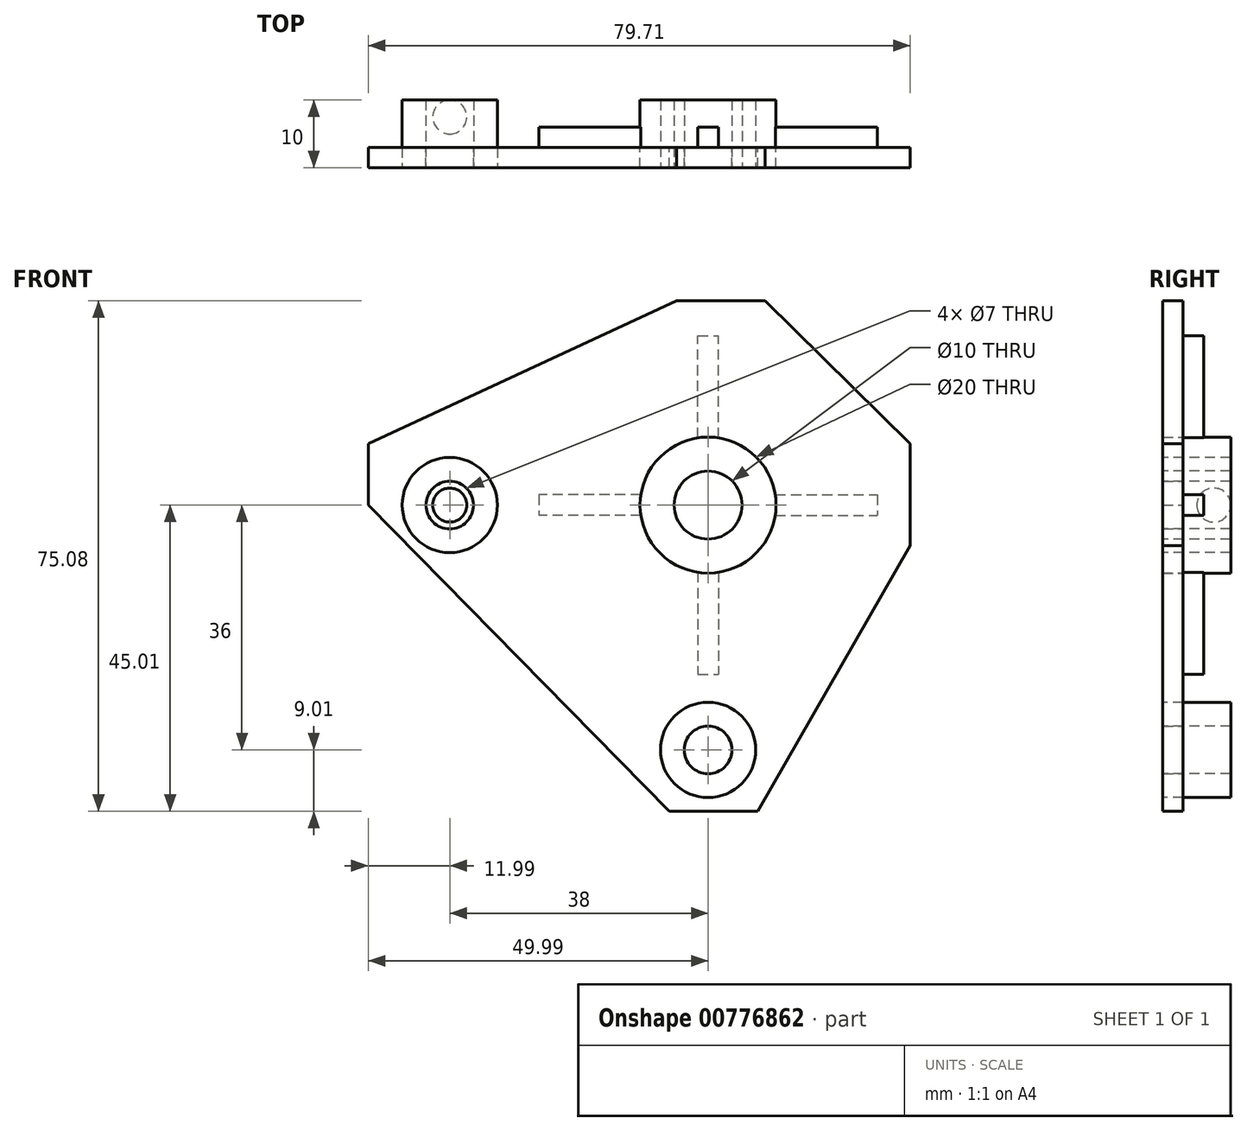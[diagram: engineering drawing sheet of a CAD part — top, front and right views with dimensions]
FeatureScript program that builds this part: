
annotation { "Feature Type Name" : "Feature", "Feature Type Description" : "" }
export const myFeature = defineFeature(function(context is Context, id is Id, definition is map)
    precondition{}
    {
        {
            var Q0;
            Q0=qCreatedBy(makeId("Front.planeOp"),FACE);
            var sketch = newSketch(context, id + "F0", { "sketchPlane" : qUnion([Q0])});
            skCircle(sketch, "E0", {"center": v(0, 0) * mm, "radius": 10 * mm});
            skLineSegment(sketch, "E1", {"start": v(0, 30.64) * mm, "end": v(0, -43.55) * mm, "construction": true});
            skLineSegment(sketch, "E2", {"start": v(-1.5, 9.89) * mm, "end": v(-1.5, 24.89) * mm});
            skLineSegment(sketch, "E3.MirrorCS", {"start": v(1.5, 9.89) * mm, "end": v(1.5, 24.89) * mm});
            skLineSegment(sketch, "E4", {"start": v(-1.5, 24.89) * mm, "end": v(1.5, 24.89) * mm});
            skLineSegment(sketch, "E5", {"start": v(-38, 0) * mm, "end": v(36.67, 0) * mm, "construction": true});
            skLineSegment(sketch, "E6.MirrorCS", {"start": v(1.5, -9.89) * mm, "end": v(1.5, -24.89) * mm});
            skLineSegment(sketch, "E7.MirrorCS", {"start": v(-1.5, -9.89) * mm, "end": v(-1.5, -24.89) * mm});
            skLineSegment(sketch, "E8.MirrorCS", {"start": v(-1.5, -24.89) * mm, "end": v(1.5, -24.89) * mm});
            skLineSegment(sketch, "E9", {"start": v(9.89, 1.5) * mm, "end": v(24.89, 1.5) * mm});
            skLineSegment(sketch, "E10.MirrorCS", {"start": v(9.89, -1.5) * mm, "end": v(24.89, -1.5) * mm});
            skLineSegment(sketch, "E11", {"start": v(24.89, 1.5) * mm, "end": v(24.89, -1.5) * mm});
            skLineSegment(sketch, "E12.MirrorCS", {"start": v(-9.89, 1.5) * mm, "end": v(-24.89, 1.5) * mm});
            skLineSegment(sketch, "E13.MirrorCS", {"start": v(-9.89, -1.5) * mm, "end": v(-24.89, -1.5) * mm});
            skLineSegment(sketch, "E14.MirrorCS", {"start": v(-24.89, 1.5) * mm, "end": v(-24.89, -1.5) * mm});
            skCircle(sketch, "E15", {"center": v(-38, 0) * mm, "radius": 3.5 * mm});
            skCircle(sketch, "E16", {"center": v(0, -36) * mm, "radius": 3.5 * mm});
            skLineSegment(sketch, "E17", {"start": v(-49.99, 0) * mm, "end": v(-5.7, -45.01) * mm});
            skLineSegment(sketch, "E18", {"start": v(-5.7, -45.01) * mm, "end": v(7.3, -45.01) * mm});
            skLineSegment(sketch, "E19", {"start": v(7.3, -45.01) * mm, "end": v(29.72, -6) * mm});
            skLineSegment(sketch, "E20", {"start": v(29.72, 2.8) * mm, "end": v(29.72, 9) * mm});
            skLineSegment(sketch, "E21", {"start": v(29.72, 9) * mm, "end": v(8.36, 30.07) * mm});
            skLineSegment(sketch, "E22", {"start": v(8.36, 30.07) * mm, "end": v(-4.64, 30.07) * mm});
            skLineSegment(sketch, "E23", {"start": v(-4.64, 30.07) * mm, "end": v(-49.99, 9) * mm});
            skLineSegment(sketch, "E24", {"start": v(-49.99, 9) * mm, "end": v(-49.99, 0) * mm});
            skLineSegment(sketch, "E25", {"start": v(29.72, 2.8) * mm, "end": v(29.72, -6) * mm});
            skSolve(sketch);
        }
        {
            var Q0;
            {var subQ0=sQuery(id+"F0.wireOp",EDGE,"E12.MirrorCS");Q0=makeQuery(id+"F0.imprint","IMPRINT",FACE,{"disambiguationData":[TD([[makeQuery(id+"F0.imprint","IMPRINT",EDGE,{"derivedFrom":subQ0}),1.0]])]});}
            var Q1;
            {var subQ0=sQuery(id+"F0.wireOp",EDGE,"E2");Q1=makeQuery(id+"F0.imprint","IMPRINT",FACE,{"disambiguationData":[TD([[makeQuery(id+"F0.imprint","IMPRINT",EDGE,{"derivedFrom":subQ0}),-1.0]])]});}
            var Q2;
            {var subQ0=sQuery(id+"F0.wireOp",EDGE,"E9");Q2=makeQuery(id+"F0.imprint","IMPRINT",FACE,{"disambiguationData":[TD([[makeQuery(id+"F0.imprint","IMPRINT",EDGE,{"derivedFrom":subQ0}),-1.0]])]});}
            var Q3;
            {var subQ0=sQuery(id+"F0.wireOp",EDGE,"E6.MirrorCS");Q3=makeQuery(id+"F0.imprint","IMPRINT",FACE,{"disambiguationData":[TD([[makeQuery(id+"F0.imprint","IMPRINT",EDGE,{"derivedFrom":subQ0}),-1.0]])]});}
            extrude(context, id + "F1", {"entities" : qUnion([Q0, Q1, Q2, Q3]), "depth" : -3 * mm, "offsetDistance" : 25 * mm});
        }
        {
            var Q0;
            {var subQ7=sQuery(id+"F0.wireOp",EDGE,"E2");Q0=makeQuery(id+"F0.imprint","IMPRINT",FACE,{"disambiguationData":[TD([[makeQuery(id+"F0.imprint","IMPRINT",EDGE,{"derivedFrom":subQ7}),1.0]])]});}
            var Q1;
            {var subQ0=sQuery(id+"F0.wireOp",EDGE,"E12.MirrorCS");Q1=makeQuery(id+"F0.imprint","IMPRINT",FACE,{"disambiguationData":[TD([[makeQuery(id+"F0.imprint","IMPRINT",EDGE,{"derivedFrom":subQ0}),1.0]])]});}
            var Q2;
            {var subQ0=sQuery(id+"F0.wireOp",EDGE,"E2");Q2=makeQuery(id+"F0.imprint","IMPRINT",FACE,{"disambiguationData":[TD([[makeQuery(id+"F0.imprint","IMPRINT",EDGE,{"derivedFrom":subQ0}),-1.0]])]});}
            var Q3;
            {var subQ0=sQuery(id+"F0.wireOp",EDGE,"E9");Q3=makeQuery(id+"F0.imprint","IMPRINT",FACE,{"disambiguationData":[TD([[makeQuery(id+"F0.imprint","IMPRINT",EDGE,{"derivedFrom":subQ0}),-1.0]])]});}
            var Q4;
            {var subQ0=sQuery(id+"F0.wireOp",EDGE,"E6.MirrorCS");Q4=makeQuery(id+"F0.imprint","IMPRINT",FACE,{"disambiguationData":[TD([[makeQuery(id+"F0.imprint","IMPRINT",EDGE,{"derivedFrom":subQ0}),-1.0]])]});}
            extrude(context, id + "F2", {"entities" : qUnion([Q0, Q1, Q2, Q3, Q4]), "depth" : 3 * mm, "offsetDistance" : 25 * mm});
        }
        {
            var Q0;
            Q0=makeQuery(id+"F2.opExtrude","CAP_FACE",FACE,{"disambiguationData":[OSD([sQuery(id+"F0.wireOp",EDGE,"E0"),sQuery(id+"F0.wireOp",EDGE,"E15"),sQuery(id+"F0.wireOp",EDGE,"E16"),sQuery(id+"F0.wireOp",EDGE,"E17"),sQuery(id+"F0.wireOp",EDGE,"E18"),sQuery(id+"F0.wireOp",EDGE,"E19"),sQuery(id+"F0.wireOp",EDGE,"E20"),sQuery(id+"F0.wireOp",EDGE,"E21"),sQuery(id+"F0.wireOp",EDGE,"E22"),sQuery(id+"F0.wireOp",EDGE,"E23"),sQuery(id+"F0.wireOp",EDGE,"E24"),sQuery(id+"F0.wireOp",EDGE,"E25")])],"isStart":false});
            var sketch = newSketch(context, id + "F3", { "sketchPlane" : qUnion([Q0])});
            skCircle(sketch, "E26", {"center": v(0, 0) * mm, "radius": 10 * mm});
            skPoint(sketch, "E26.first.point", {"position": v(9.22, 3.86) * mm});
            skPoint(sketch, "E26.second.point", {"position": v(-9.23, -3.84) * mm});
            skPoint(sketch, "E26.third.point", {"position": v(2.28, -9.74) * mm});
            skCircle(sketch, "E27.0", {"center": v(0, 0) * mm, "radius": 5 * mm});
            skCircle(sketch, "E28.0", {"center": v(-38, 0) * mm, "radius": 7 * mm});
            skCircle(sketch, "E29.0", {"center": v(0, -36) * mm, "radius": 7 * mm});
            skSolve(sketch);
        }
        {
            var Q0;
            Q0=makeQuery(id+"F3.imprint","IMPRINT",FACE,{"disambiguationData":[TD([[makeQuery(id+"F3.imprint","IMPRINT",EDGE,{"derivedFrom":sQuery(id+"F3.wireOp",EDGE,"E26")}),1.0]])]});
            var Q1;
            Q1=makeQuery(id+"F3.imprint","IMPRINT",FACE,{"disambiguationData":[TD([[makeQuery(id+"F3.imprint","IMPRINT",EDGE,{"derivedFrom":sQuery(id+"F3.wireOp",EDGE,"E29.0")}),1.0]])]});
            var Q2;
            Q2=makeQuery(id+"F3.imprint","IMPRINT",FACE,{"disambiguationData":[TD([[makeQuery(id+"F3.imprint","IMPRINT",EDGE,{"derivedFrom":sQuery(id+"F3.wireOp",EDGE,"E28.0")}),1.0]])]});
            extrude(context, id + "F4", {"entities" : qUnion([Q0, Q1, Q2]), "depth" : -10 * mm, "offsetDistance" : 25 * mm});
        }
        {
            var Q0;
            Q0=qCreatedBy(makeId("Top.planeOp"),FACE);
            var sketch = newSketch(context, id + "F5", { "sketchPlane" : qUnion([Q0])});
            skLineSegment(sketch, "E30", {"start": v(-38, 3258.99) * mm, "end": v(-38, -2682.6) * mm, "construction": true});
            skLineSegment(sketch, "E31", {"start": v(-38, 7) * mm, "end": v(-38, 2) * mm});
            skArc(sketch, "E32", {"start": v(-38, 2) * mm, "mid": v(-35.5, 4.5) * mm, "end": v(-38, 7) * mm});
            skSolve(sketch);
        }
        {
            var Q0;
            Q0=makeQuery(id+"F5.imprint","IMPRINT",FACE,{"disambiguationData":[TD([[makeQuery(id+"F5.imprint","IMPRINT",EDGE,{"derivedFrom":sQuery(id+"F5.wireOp",EDGE,"E31")}),1.0]])]});
            var Q1;
            Q1=sQuery(id+"F5.wireOp",EDGE,"E31");
            revolve(context, id + "F6", {"surfaceOperationType" : NewSurfaceOperationType.NEW, "entities" : qUnion([Q0]), "axis" : qUnion([Q1]), "revolveType" : RevolveType.FULL});
        }
    });
